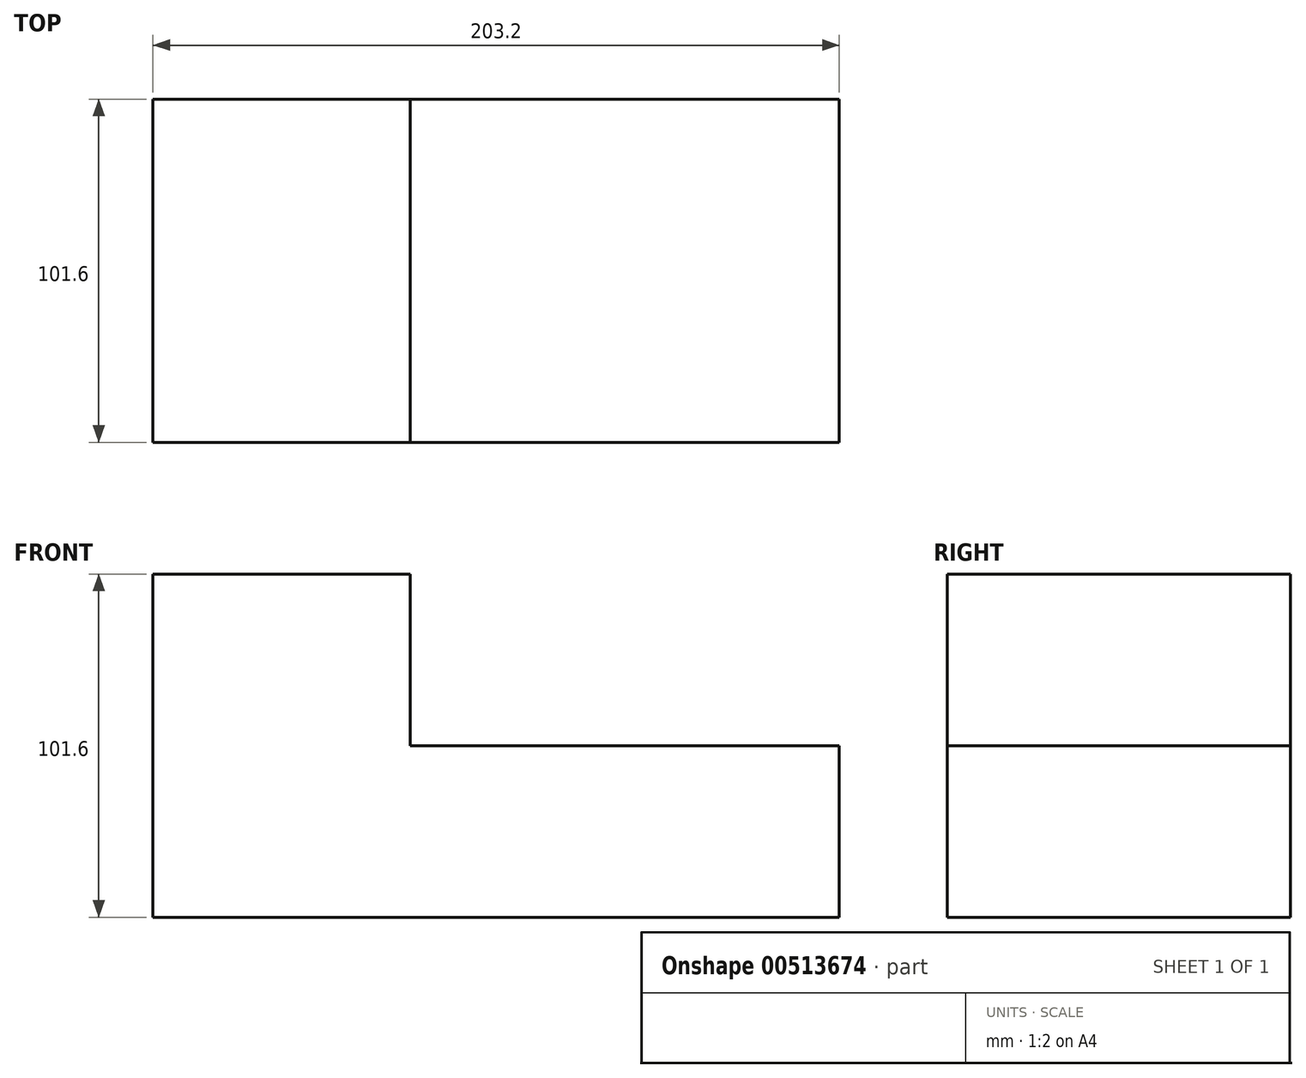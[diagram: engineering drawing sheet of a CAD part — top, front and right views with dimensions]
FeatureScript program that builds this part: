
annotation { "Feature Type Name" : "Feature", "Feature Type Description" : "" }
export const myFeature = defineFeature(function(context is Context, id is Id, definition is map)
    precondition{}
    {
        {
            var Q0;
            Q0=qCreatedBy(makeId("Front.planeOp"),FACE);
            var sketch = newSketch(context, id + "F0", { "sketchPlane" : qUnion([Q0])});
            skLineSegment(sketch, "E0.bottom", {"start": v(-95.97, 50.8) * mm, "end": v(-19.77, 50.8) * mm});
            skLineSegment(sketch, "E0.top", {"start": v(-95.97, -50.8) * mm, "end": v(107.23, -50.8) * mm});
            skLineSegment(sketch, "E0.left", {"start": v(-95.97, 50.8) * mm, "end": v(-95.97, -50.8) * mm});
            skLineSegment(sketch, "E1", {"start": v(107.23, 0) * mm, "end": v(107.23, -50.8) * mm});
            skLineSegment(sketch, "E2", {"start": v(-19.77, 50.8) * mm, "end": v(-19.77, 0) * mm});
            skLineSegment(sketch, "E3", {"start": v(-19.77, 0) * mm, "end": v(107.23, 0) * mm});
            skSolve(sketch);
        }
        {
            var Q0;
            Q0 = qSketchRegion(id + "F0", true);
            extrude(context, id + "F1", {"entities" : qUnion([Q0]), "depth" : 101.6 * mm});
        }
    });
